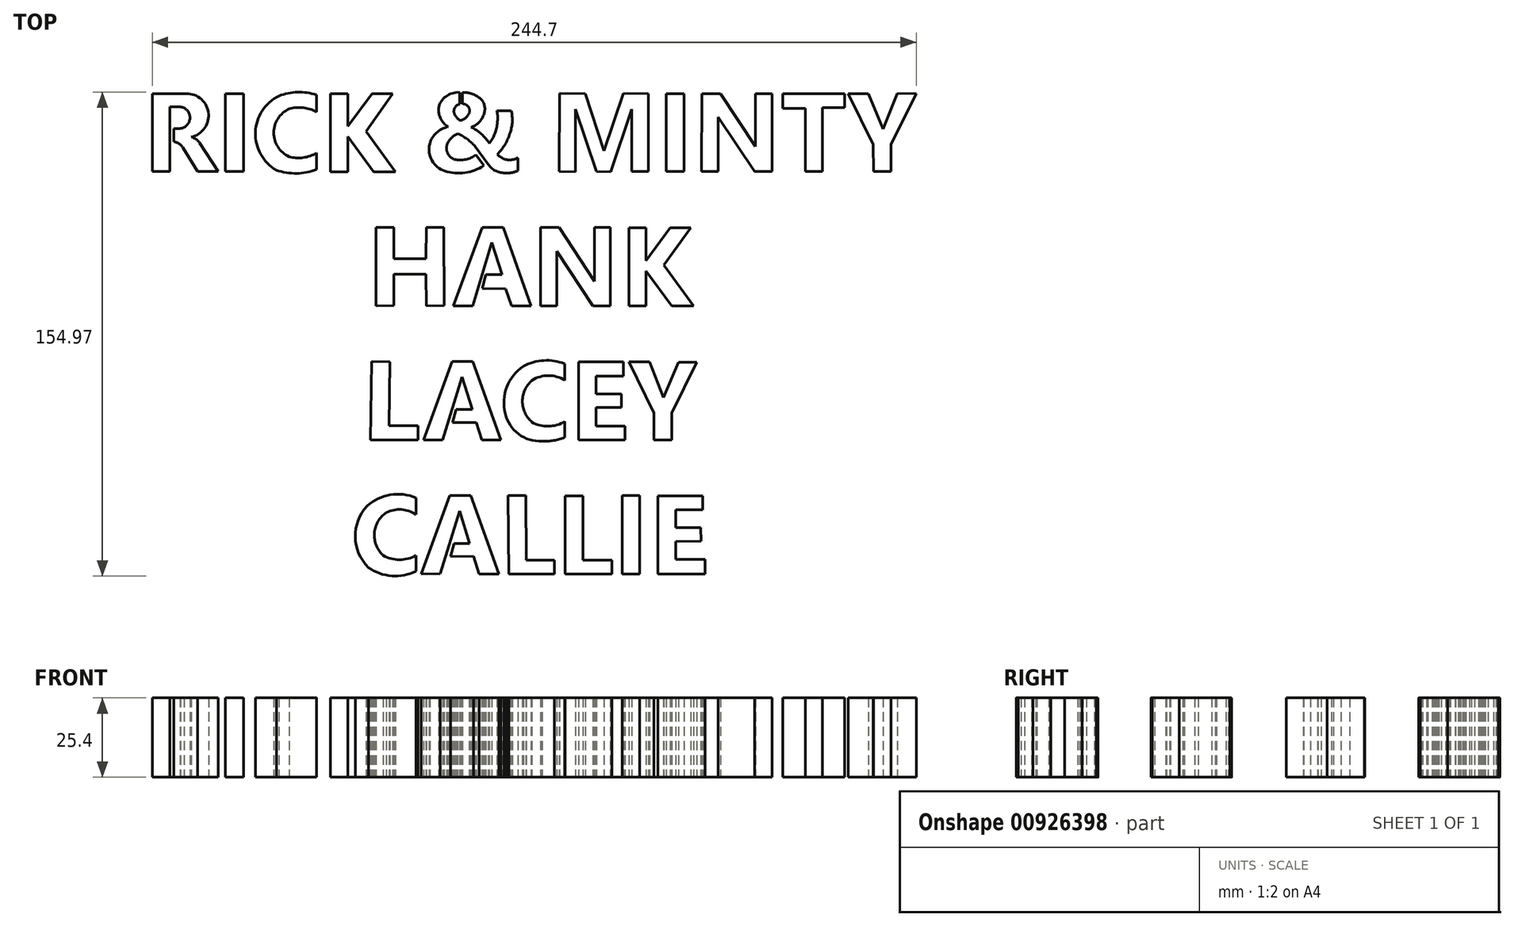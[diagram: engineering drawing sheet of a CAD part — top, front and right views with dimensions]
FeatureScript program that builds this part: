
annotation { "Feature Type Name" : "Feature", "Feature Type Description" : "" }
export const myFeature = defineFeature(function(context is Context, id is Id, definition is map)
    precondition{}
    {
        {
            var Q0;
            Q0=qCreatedBy(makeId("Top.planeOp"),FACE);
            var sketch = newSketch(context, id + "F0", { "sketchPlane" : qUnion([Q0])});
            skLineSegment(sketch, "E0.bottom", {"start": v(49.51, 242.62) * mm, "end": v(55.44, 242.62) * mm});
            skLineSegment(sketch, "E0.top", {"start": v(49.51, 267.6) * mm, "end": v(55.44, 267.6) * mm});
            skLineSegment(sketch, "E0.left", {"start": v(49.51, 242.62) * mm, "end": v(49.51, 267.6) * mm});
            skLineSegment(sketch, "E0.right", {"start": v(55.44, 242.62) * mm, "end": v(55.44, 267.6) * mm});
            skLineSegment(sketch, "E1.bottom", {"start": v(190.8, 242.61) * mm, "end": v(196.47, 242.61) * mm});
            skLineSegment(sketch, "E1.top", {"start": v(190.8, 267.6) * mm, "end": v(196.47, 267.6) * mm});
            skLineSegment(sketch, "E1.left", {"start": v(190.8, 242.61) * mm, "end": v(190.8, 267.6) * mm});
            skLineSegment(sketch, "E1.right", {"start": v(196.47, 242.61) * mm, "end": v(196.47, 267.6) * mm});
            skLineSegment(sketch, "E2.bottom", {"start": v(176.67, 138.96) * mm, "end": v(182.27, 138.96) * mm});
            skLineSegment(sketch, "E2.top", {"start": v(176.67, 113.81) * mm, "end": v(182.27, 113.81) * mm});
            skLineSegment(sketch, "E2.left", {"start": v(176.67, 138.96) * mm, "end": v(176.67, 113.81) * mm});
            skLineSegment(sketch, "E2.right", {"start": v(182.27, 138.96) * mm, "end": v(182.27, 113.81) * mm});
            skLineSegment(sketch, "E3", {"start": v(47.25, 242.62) * mm, "end": v(41.25, 251.83) * mm});
            skLineSegment(sketch, "E4", {"start": v(47.25, 242.62) * mm, "end": v(40.7, 242.62) * mm});
            skLineSegment(sketch, "E5", {"start": v(40.7, 242.62) * mm, "end": v(36, 250.26) * mm});
            skLineSegment(sketch, "E6", {"start": v(33.02, 256.44) * mm, "end": v(33.02, 252.2) * mm});
            skLineSegment(sketch, "E7", {"start": v(31.77, 242.62) * mm, "end": v(31.77, 263.35) * mm});
            skLineSegment(sketch, "E8", {"start": v(31.77, 263.35) * mm, "end": v(35.19, 263.35) * mm});
            skLineSegment(sketch, "E9", {"start": v(33.02, 256.44) * mm, "end": v(35.02, 256.44) * mm});
            skLineSegment(sketch, "E10", {"start": v(31.77, 242.62) * mm, "end": v(26.18, 242.62) * mm});
            skLineSegment(sketch, "E11", {"start": v(26.18, 242.62) * mm, "end": v(26.18, 267.53) * mm});
            skLineSegment(sketch, "E12", {"start": v(26.18, 267.53) * mm, "end": v(36.34, 267.53) * mm});
            skArc(sketch, "E13", {"start": v(35.02, 256.44) * mm, "mid": v(38.21, 259.82) * mm, "end": v(35.19, 263.35) * mm});
            skArc(sketch, "E14", {"start": v(36, 250.26) * mm, "mid": v(34.72, 251.56) * mm, "end": v(33.02, 252.2) * mm});
            skArc(sketch, "E15", {"start": v(41.25, 251.83) * mm, "mid": v(40.1, 253.02) * mm, "end": v(38.58, 253.7) * mm});
            skArc(sketch, "E16", {"start": v(38.58, 253.7) * mm, "mid": v(44.09, 261.7) * mm, "end": v(36.34, 267.53) * mm});
            skArc(sketch, "E17", {"start": v(78.78, 261.7) * mm, "mid": v(74.5, 263.08) * mm, "end": v(70, 262.7) * mm});
            skPoint(sketch, "E17.startSnap0", {"position": v(44.09, 261.7) * mm});
            skArc(sketch, "E18", {"start": v(69.97, 247.4) * mm, "mid": v(74.48, 247.08) * mm, "end": v(78.74, 248.57) * mm});
            skArc(sketch, "E19", {"start": v(70, 262.7) * mm, "mid": v(65.06, 255.06) * mm, "end": v(69.97, 247.4) * mm});
            skArc(sketch, "E20", {"start": v(78.78, 267.16) * mm, "mid": v(72.7, 268.07) * mm, "end": v(66.69, 266.85) * mm});
            skArc(sketch, "E21", {"start": v(65.9, 243.08) * mm, "mid": v(72.34, 242.05) * mm, "end": v(78.74, 243.32) * mm});
            skArc(sketch, "E22", {"start": v(66.69, 266.85) * mm, "mid": v(59.2, 255.2) * mm, "end": v(65.9, 243.08) * mm});
            skLineSegment(sketch, "E23", {"start": v(83.22, 242.5) * mm, "end": v(83.22, 267.52) * mm});
            skLineSegment(sketch, "E24", {"start": v(83.22, 267.52) * mm, "end": v(88.85, 267.52) * mm});
            skLineSegment(sketch, "E25", {"start": v(88.85, 267.52) * mm, "end": v(88.85, 257.13) * mm});
            skLineSegment(sketch, "E26", {"start": v(88.85, 257.13) * mm, "end": v(96.57, 267.52) * mm});
            skLineSegment(sketch, "E27", {"start": v(96.57, 267.52) * mm, "end": v(103.18, 267.52) * mm});
            skLineSegment(sketch, "E28", {"start": v(103.18, 267.52) * mm, "end": v(94.58, 255.52) * mm});
            skLineSegment(sketch, "E29", {"start": v(94.58, 255.52) * mm, "end": v(103.97, 242.54) * mm});
            skLineSegment(sketch, "E30", {"start": v(103.97, 242.54) * mm, "end": v(96.98, 242.54) * mm});
            skLineSegment(sketch, "E31", {"start": v(96.98, 242.54) * mm, "end": v(88.85, 253.87) * mm});
            skLineSegment(sketch, "E32", {"start": v(88.85, 253.87) * mm, "end": v(88.85, 242.54) * mm});
            skLineSegment(sketch, "E33", {"start": v(88.85, 242.54) * mm, "end": v(83.22, 242.5) * mm});
            skLineSegment(sketch, "E34", {"start": v(124.56, 267.99) * mm, "end": v(124.56, 264.22) * mm});
            skLineSegment(sketch, "E35", {"start": v(125.46, 264.31) * mm, "end": v(125.46, 267.97) * mm});
            skArc(sketch, "E36", {"start": v(124.56, 264.22) * mm, "mid": v(123.16, 263.23) * mm, "end": v(122.77, 261.55) * mm});
            skArc(sketch, "E37", {"start": v(122.77, 261.55) * mm, "mid": v(123.56, 260.05) * mm, "end": v(124.9, 259) * mm});
            skArc(sketch, "E38", {"start": v(124.9, 259) * mm, "mid": v(126.57, 259.83) * mm, "end": v(127.66, 261.36) * mm});
            skArc(sketch, "E39", {"start": v(127.66, 261.36) * mm, "mid": v(127.35, 263.42) * mm, "end": v(125.46, 264.31) * mm});
            skArc(sketch, "E40", {"start": v(124.56, 267.99) * mm, "mid": v(120.28, 266.72) * mm, "end": v(117.83, 262.98) * mm});
            skArc(sketch, "E41", {"start": v(117.83, 262.98) * mm, "mid": v(118.54, 259.55) * mm, "end": v(120.89, 256.95) * mm});
            skArc(sketch, "E42", {"start": v(120.89, 256.95) * mm, "mid": v(117.2, 255.07) * mm, "end": v(115.03, 251.53) * mm});
            skArc(sketch, "E43", {"start": v(115.03, 251.53) * mm, "mid": v(115.71, 246.16) * mm, "end": v(119.92, 242.76) * mm});
            skArc(sketch, "E44", {"start": v(119.92, 242.76) * mm, "mid": v(126.33, 242.25) * mm, "end": v(132.34, 244.55) * mm});
            skArc(sketch, "E45", {"start": v(123, 246.5) * mm, "mid": v(126.56, 246.51) * mm, "end": v(129.83, 247.96) * mm});
            skArc(sketch, "E46", {"start": v(120.66, 251.53) * mm, "mid": v(120.74, 248.51) * mm, "end": v(123, 246.5) * mm});
            skArc(sketch, "E47", {"start": v(124.03, 254.74) * mm, "mid": v(122.03, 253.47) * mm, "end": v(120.66, 251.53) * mm});
            skArc(sketch, "E48", {"start": v(129.56, 250.7) * mm, "mid": v(127.01, 253.03) * mm, "end": v(124.03, 254.74) * mm});
            skArc(sketch, "E49", {"start": v(133.72, 244.95) * mm, "mid": v(136.04, 242.9) * mm, "end": v(139.05, 242.2) * mm});
            skArc(sketch, "E50", {"start": v(139.05, 242.2) * mm, "mid": v(141.22, 242.27) * mm, "end": v(143.28, 242.95) * mm});
            skArc(sketch, "E51", {"start": v(139.26, 246.5) * mm, "mid": v(141.33, 246.42) * mm, "end": v(143.3, 247.04) * mm});
            skArc(sketch, "E52", {"start": v(136.65, 248.15) * mm, "mid": v(137.86, 247.18) * mm, "end": v(139.26, 246.5) * mm});
            skArc(sketch, "E53", {"start": v(136.65, 248.15) * mm, "mid": v(139.18, 251.4) * mm, "end": v(140.82, 255.2) * mm});
            skArc(sketch, "E54", {"start": v(140.82, 255.2) * mm, "mid": v(141.46, 258.62) * mm, "end": v(141.14, 262.1) * mm});
            skArc(sketch, "E55", {"start": v(136.65, 258.32) * mm, "mid": v(136.78, 260.23) * mm, "end": v(136.5, 262.12) * mm});
            skArc(sketch, "E56", {"start": v(134.13, 251.69) * mm, "mid": v(135.89, 254.81) * mm, "end": v(136.65, 258.32) * mm});
            skArc(sketch, "E57", {"start": v(134.13, 251.69) * mm, "mid": v(131.57, 254.64) * mm, "end": v(128.31, 256.82) * mm});
            skArc(sketch, "E58", {"start": v(128.31, 256.82) * mm, "mid": v(130.9, 258.48) * mm, "end": v(132.42, 261.17) * mm});
            skArc(sketch, "E59", {"start": v(132.42, 261.17) * mm, "mid": v(132.55, 263.85) * mm, "end": v(131.1, 266.1) * mm});
            skArc(sketch, "E60", {"start": v(131.1, 266.1) * mm, "mid": v(128.45, 267.55) * mm, "end": v(125.46, 267.97) * mm});
            skLineSegment(sketch, "E61", {"start": v(129.83, 247.96) * mm, "end": v(132.34, 244.55) * mm});
            skLineSegment(sketch, "E62", {"start": v(129.56, 250.7) * mm, "end": v(133.72, 244.95) * mm});
            skLineSegment(sketch, "E63", {"start": v(143.28, 242.95) * mm, "end": v(143.3, 247.04) * mm});
            skLineSegment(sketch, "E64", {"start": v(136.5, 262.12) * mm, "end": v(141.14, 262.1) * mm});
            skLineSegment(sketch, "E65", {"start": v(185.07, 242.61) * mm, "end": v(185.07, 267.6) * mm});
            skLineSegment(sketch, "E66", {"start": v(185.07, 267.6) * mm, "end": v(177.1, 267.62) * mm});
            skLineSegment(sketch, "E67", {"start": v(177.1, 267.62) * mm, "end": v(170.85, 249.3) * mm});
            skLineSegment(sketch, "E68", {"start": v(170.85, 249.3) * mm, "end": v(164.84, 267.6) * mm});
            skLineSegment(sketch, "E69", {"start": v(164.84, 267.6) * mm, "end": v(156.64, 267.62) * mm});
            skLineSegment(sketch, "E70", {"start": v(156.64, 267.62) * mm, "end": v(156.54, 242.61) * mm});
            skLineSegment(sketch, "E71", {"start": v(156.54, 242.61) * mm, "end": v(161.72, 242.6) * mm});
            skLineSegment(sketch, "E72", {"start": v(161.72, 242.6) * mm, "end": v(161.72, 262.64) * mm});
            skLineSegment(sketch, "E73", {"start": v(161.72, 262.64) * mm, "end": v(168.36, 242.61) * mm});
            skLineSegment(sketch, "E74", {"start": v(168.36, 242.61) * mm, "end": v(173, 242.6) * mm});
            skLineSegment(sketch, "E75", {"start": v(173, 242.6) * mm, "end": v(179.7, 262.64) * mm});
            skLineSegment(sketch, "E76", {"start": v(179.7, 262.64) * mm, "end": v(179.7, 242.61) * mm});
            skLineSegment(sketch, "E77", {"start": v(179.7, 242.61) * mm, "end": v(185.07, 242.61) * mm});
            skLineSegment(sketch, "E78", {"start": v(202.1, 242.61) * mm, "end": v(202.18, 267.6) * mm});
            skLineSegment(sketch, "E79", {"start": v(202.18, 267.6) * mm, "end": v(208.2, 267.57) * mm});
            skLineSegment(sketch, "E80", {"start": v(208.2, 267.57) * mm, "end": v(219.4, 250.7) * mm});
            skLineSegment(sketch, "E81", {"start": v(219.4, 250.7) * mm, "end": v(219.4, 267.6) * mm});
            skLineSegment(sketch, "E82", {"start": v(219.4, 267.6) * mm, "end": v(224.69, 267.57) * mm});
            skLineSegment(sketch, "E83", {"start": v(224.69, 267.57) * mm, "end": v(224.69, 242.61) * mm});
            skLineSegment(sketch, "E84", {"start": v(224.69, 242.61) * mm, "end": v(219.05, 242.63) * mm});
            skLineSegment(sketch, "E85", {"start": v(219.05, 242.63) * mm, "end": v(207.44, 260.02) * mm});
            skLineSegment(sketch, "E86", {"start": v(207.44, 260.02) * mm, "end": v(207.44, 242.61) * mm});
            skLineSegment(sketch, "E87", {"start": v(207.44, 242.61) * mm, "end": v(202.1, 242.61) * mm});
            skLineSegment(sketch, "E88", {"start": v(228.12, 267.6) * mm, "end": v(247.98, 267.52) * mm});
            skLineSegment(sketch, "E89", {"start": v(247.98, 267.52) * mm, "end": v(247.98, 263.1) * mm});
            skLineSegment(sketch, "E90", {"start": v(247.98, 263.1) * mm, "end": v(240.84, 263.12) * mm});
            skLineSegment(sketch, "E91", {"start": v(240.84, 263.12) * mm, "end": v(240.84, 242.61) * mm});
            skLineSegment(sketch, "E92", {"start": v(240.84, 242.61) * mm, "end": v(235.32, 242.63) * mm});
            skLineSegment(sketch, "E93", {"start": v(235.32, 242.63) * mm, "end": v(235.32, 262.86) * mm});
            skLineSegment(sketch, "E94", {"start": v(235.32, 262.86) * mm, "end": v(228.12, 262.9) * mm});
            skLineSegment(sketch, "E95", {"start": v(228.12, 262.9) * mm, "end": v(228.12, 267.6) * mm});
            skLineSegment(sketch, "E96", {"start": v(249.05, 267.57) * mm, "end": v(255.54, 267.55) * mm});
            skLineSegment(sketch, "E97", {"start": v(255.54, 267.55) * mm, "end": v(260.2, 256.2) * mm});
            skLineSegment(sketch, "E98", {"start": v(260.2, 256.2) * mm, "end": v(264.87, 267.64) * mm});
            skLineSegment(sketch, "E99", {"start": v(264.87, 267.64) * mm, "end": v(270.88, 267.57) * mm});
            skLineSegment(sketch, "E100", {"start": v(270.88, 267.57) * mm, "end": v(262.76, 251.37) * mm});
            skLineSegment(sketch, "E101", {"start": v(262.76, 251.37) * mm, "end": v(262.72, 242.6) * mm});
            skLineSegment(sketch, "E102", {"start": v(262.72, 242.6) * mm, "end": v(257.18, 242.63) * mm});
            skLineSegment(sketch, "E103", {"start": v(257.18, 242.63) * mm, "end": v(257.1, 251.32) * mm});
            skLineSegment(sketch, "E104", {"start": v(257.1, 251.32) * mm, "end": v(249.05, 267.57) * mm});
            skLineSegment(sketch, "E105", {"start": v(97.85, 199.62) * mm, "end": v(97.85, 224.72) * mm});
            skLineSegment(sketch, "E106", {"start": v(97.85, 224.72) * mm, "end": v(103.54, 224.72) * mm});
            skLineSegment(sketch, "E107", {"start": v(103.54, 224.72) * mm, "end": v(103.54, 214.72) * mm});
            skLineSegment(sketch, "E108", {"start": v(103.54, 214.72) * mm, "end": v(113.87, 214.72) * mm});
            skLineSegment(sketch, "E109", {"start": v(113.87, 214.72) * mm, "end": v(113.99, 224.72) * mm});
            skLineSegment(sketch, "E110", {"start": v(113.99, 224.72) * mm, "end": v(119.56, 224.72) * mm});
            skLineSegment(sketch, "E111", {"start": v(119.56, 224.72) * mm, "end": v(119.62, 199.68) * mm});
            skLineSegment(sketch, "E112", {"start": v(119.62, 199.68) * mm, "end": v(113.93, 199.66) * mm});
            skLineSegment(sketch, "E113", {"start": v(113.93, 199.66) * mm, "end": v(113.82, 209.73) * mm});
            skLineSegment(sketch, "E114", {"start": v(113.82, 209.73) * mm, "end": v(103.54, 209.78) * mm});
            skLineSegment(sketch, "E115", {"start": v(103.54, 209.78) * mm, "end": v(103.48, 199.68) * mm});
            skLineSegment(sketch, "E116", {"start": v(103.48, 199.68) * mm, "end": v(97.85, 199.62) * mm});
            skLineSegment(sketch, "E117", {"start": v(122.6, 199.62) * mm, "end": v(131.8, 224.72) * mm});
            skLineSegment(sketch, "E118", {"start": v(131.8, 224.72) * mm, "end": v(138.51, 224.72) * mm});
            skLineSegment(sketch, "E119", {"start": v(138.51, 224.72) * mm, "end": v(147.41, 199.62) * mm});
            skLineSegment(sketch, "E120", {"start": v(147.41, 199.62) * mm, "end": v(141.21, 199.62) * mm});
            skLineSegment(sketch, "E121", {"start": v(141.21, 199.62) * mm, "end": v(139.37, 205.13) * mm});
            skLineSegment(sketch, "E122", {"start": v(139.37, 205.13) * mm, "end": v(131.9, 205.25) * mm});
            skLineSegment(sketch, "E123", {"start": v(131.9, 205.25) * mm, "end": v(133, 209.61) * mm});
            skLineSegment(sketch, "E124", {"start": v(133, 209.61) * mm, "end": v(138.17, 209.61) * mm});
            skLineSegment(sketch, "E125", {"start": v(138.17, 209.61) * mm, "end": v(134.84, 219.95) * mm});
            skLineSegment(sketch, "E126", {"start": v(134.84, 219.95) * mm, "end": v(128.75, 199.62) * mm});
            skLineSegment(sketch, "E127", {"start": v(128.75, 199.62) * mm, "end": v(122.6, 199.62) * mm});
            skLineSegment(sketch, "E128", {"start": v(150.46, 199.62) * mm, "end": v(150.46, 224.72) * mm});
            skLineSegment(sketch, "E129", {"start": v(150.46, 224.72) * mm, "end": v(156.49, 224.72) * mm});
            skLineSegment(sketch, "E130", {"start": v(156.49, 224.72) * mm, "end": v(167.74, 207.43) * mm});
            skLineSegment(sketch, "E131", {"start": v(167.74, 207.43) * mm, "end": v(167.74, 224.72) * mm});
            skLineSegment(sketch, "E132", {"start": v(167.74, 224.72) * mm, "end": v(172.86, 224.72) * mm});
            skLineSegment(sketch, "E133", {"start": v(172.86, 224.72) * mm, "end": v(172.86, 199.62) * mm});
            skLineSegment(sketch, "E134", {"start": v(172.86, 199.62) * mm, "end": v(167.28, 199.62) * mm});
            skLineSegment(sketch, "E135", {"start": v(167.28, 199.62) * mm, "end": v(155.68, 217.2) * mm});
            skLineSegment(sketch, "E136", {"start": v(155.68, 217.2) * mm, "end": v(155.68, 199.62) * mm});
            skLineSegment(sketch, "E137", {"start": v(155.68, 199.62) * mm, "end": v(150.46, 199.62) * mm});
            skLineSegment(sketch, "E138", {"start": v(178.77, 199.62) * mm, "end": v(178.77, 224.66) * mm});
            skLineSegment(sketch, "E139", {"start": v(178.77, 224.66) * mm, "end": v(184.34, 224.66) * mm});
            skLineSegment(sketch, "E140", {"start": v(184.34, 224.66) * mm, "end": v(184.34, 214.15) * mm});
            skLineSegment(sketch, "E141", {"start": v(184.34, 214.15) * mm, "end": v(191.98, 224.6) * mm});
            skLineSegment(sketch, "E142", {"start": v(191.98, 224.6) * mm, "end": v(198.7, 224.6) * mm});
            skLineSegment(sketch, "E143", {"start": v(198.7, 224.6) * mm, "end": v(189.97, 212.71) * mm});
            skLineSegment(sketch, "E144", {"start": v(189.97, 212.71) * mm, "end": v(199.56, 199.62) * mm});
            skLineSegment(sketch, "E145", {"start": v(199.56, 199.62) * mm, "end": v(192.55, 199.62) * mm});
            skLineSegment(sketch, "E146", {"start": v(192.55, 199.62) * mm, "end": v(184.34, 210.82) * mm});
            skLineSegment(sketch, "E147", {"start": v(184.34, 210.82) * mm, "end": v(184.34, 199.62) * mm});
            skLineSegment(sketch, "E148", {"start": v(184.34, 199.62) * mm, "end": v(178.77, 199.62) * mm});
            skLineSegment(sketch, "E149", {"start": v(78.74, 243.32) * mm, "end": v(78.74, 248.57) * mm});
            skLineSegment(sketch, "E150", {"start": v(78.78, 267.16) * mm, "end": v(78.78, 261.7) * mm});
            skLineSegment(sketch, "E151", {"start": v(96.37, 181.8) * mm, "end": v(96.08, 156.74) * mm});
            skLineSegment(sketch, "E152", {"start": v(96.08, 156.74) * mm, "end": v(111.33, 156.74) * mm});
            skLineSegment(sketch, "E153", {"start": v(111.33, 156.74) * mm, "end": v(111.28, 161.25) * mm});
            skLineSegment(sketch, "E154", {"start": v(111.28, 161.25) * mm, "end": v(101.97, 161.25) * mm});
            skLineSegment(sketch, "E155", {"start": v(101.97, 161.25) * mm, "end": v(102.2, 181.67) * mm});
            skLineSegment(sketch, "E156", {"start": v(102.2, 181.67) * mm, "end": v(96.37, 181.8) * mm});
            skLineSegment(sketch, "E157", {"start": v(113.07, 156.74) * mm, "end": v(122.25, 181.8) * mm});
            skLineSegment(sketch, "E158", {"start": v(122.25, 181.8) * mm, "end": v(128.83, 181.8) * mm});
            skLineSegment(sketch, "E159", {"start": v(128.83, 181.8) * mm, "end": v(137.8, 156.74) * mm});
            skLineSegment(sketch, "E160", {"start": v(137.8, 156.74) * mm, "end": v(131.71, 156.74) * mm});
            skLineSegment(sketch, "E161", {"start": v(131.71, 156.74) * mm, "end": v(129.92, 162.26) * mm});
            skLineSegment(sketch, "E162", {"start": v(129.92, 162.26) * mm, "end": v(122.35, 162.26) * mm});
            skLineSegment(sketch, "E163", {"start": v(122.35, 162.26) * mm, "end": v(123.4, 166.47) * mm});
            skLineSegment(sketch, "E164", {"start": v(123.4, 166.47) * mm, "end": v(128.62, 166.47) * mm});
            skLineSegment(sketch, "E165", {"start": v(128.62, 166.47) * mm, "end": v(125.32, 176.89) * mm});
            skLineSegment(sketch, "E166", {"start": v(125.32, 176.89) * mm, "end": v(119.15, 156.74) * mm});
            skLineSegment(sketch, "E167", {"start": v(119.15, 156.74) * mm, "end": v(113.07, 156.74) * mm});
            skLineSegment(sketch, "E168", {"start": v(158.3, 175.78) * mm, "end": v(158.24, 181.1) * mm});
            skLineSegment(sketch, "E169", {"start": v(158.3, 162.6) * mm, "end": v(158.3, 157.51) * mm});
            skArc(sketch, "E170", {"start": v(158.3, 175.78) * mm, "mid": v(153.05, 177.3) * mm, "end": v(147.79, 175.78) * mm});
            skArc(sketch, "E171", {"start": v(147.79, 175.78) * mm, "mid": v(144.7, 169.09) * mm, "end": v(147.79, 162.4) * mm});
            skArc(sketch, "E172", {"start": v(147.79, 162.4) * mm, "mid": v(153.07, 161.07) * mm, "end": v(158.3, 162.6) * mm});
            skArc(sketch, "E173", {"start": v(158.24, 181.1) * mm, "mid": v(151.57, 182.13) * mm, "end": v(145.06, 180.32) * mm});
            skArc(sketch, "E174", {"start": v(145.06, 180.32) * mm, "mid": v(139.73, 173.67) * mm, "end": v(139.25, 165.16) * mm});
            skArc(sketch, "E175", {"start": v(139.25, 165.16) * mm, "mid": v(143.48, 158.56) * mm, "end": v(151, 156.32) * mm});
            skArc(sketch, "E176", {"start": v(151, 156.32) * mm, "mid": v(154.71, 156.53) * mm, "end": v(158.3, 157.51) * mm});
            skLineSegment(sketch, "E177", {"start": v(162.68, 156.66) * mm, "end": v(162.68, 181.69) * mm});
            skLineSegment(sketch, "E178", {"start": v(162.68, 181.69) * mm, "end": v(177.09, 181.69) * mm});
            skLineSegment(sketch, "E179", {"start": v(177.09, 181.69) * mm, "end": v(177.09, 177.11) * mm});
            skLineSegment(sketch, "E180", {"start": v(177.09, 177.11) * mm, "end": v(168.31, 177.11) * mm});
            skLineSegment(sketch, "E181", {"start": v(168.31, 177.11) * mm, "end": v(168.31, 171.38) * mm});
            skLineSegment(sketch, "E182", {"start": v(168.31, 171.38) * mm, "end": v(176.44, 171.38) * mm});
            skLineSegment(sketch, "E183", {"start": v(176.44, 171.38) * mm, "end": v(176.44, 167.04) * mm});
            skLineSegment(sketch, "E184", {"start": v(176.44, 167.04) * mm, "end": v(168.31, 167.04) * mm});
            skLineSegment(sketch, "E185", {"start": v(168.31, 167.04) * mm, "end": v(168.31, 161.17) * mm});
            skLineSegment(sketch, "E186", {"start": v(168.31, 161.17) * mm, "end": v(177.57, 161.17) * mm});
            skLineSegment(sketch, "E187", {"start": v(177.57, 161.17) * mm, "end": v(177.57, 156.7) * mm});
            skLineSegment(sketch, "E188", {"start": v(177.57, 156.7) * mm, "end": v(162.68, 156.66) * mm});
            skLineSegment(sketch, "E189", {"start": v(186.85, 156.66) * mm, "end": v(186.85, 165.33) * mm});
            skLineSegment(sketch, "E190", {"start": v(186.85, 165.33) * mm, "end": v(178.86, 181.66) * mm});
            skLineSegment(sketch, "E191", {"start": v(178.86, 181.66) * mm, "end": v(185.39, 181.66) * mm});
            skLineSegment(sketch, "E192", {"start": v(185.39, 181.66) * mm, "end": v(189.93, 170.28) * mm});
            skLineSegment(sketch, "E193", {"start": v(189.93, 170.28) * mm, "end": v(194.67, 181.62) * mm});
            skLineSegment(sketch, "E194", {"start": v(194.67, 181.62) * mm, "end": v(200.58, 181.62) * mm});
            skLineSegment(sketch, "E195", {"start": v(200.58, 181.62) * mm, "end": v(192.49, 165.37) * mm});
            skLineSegment(sketch, "E196", {"start": v(192.49, 165.37) * mm, "end": v(192.49, 156.66) * mm});
            skLineSegment(sketch, "E197", {"start": v(192.49, 156.66) * mm, "end": v(186.85, 156.66) * mm});
            skLineSegment(sketch, "E198", {"start": v(188.15, 113.81) * mm, "end": v(188.1, 138.73) * mm});
            skLineSegment(sketch, "E199", {"start": v(188.1, 138.73) * mm, "end": v(202.5, 138.76) * mm});
            skLineSegment(sketch, "E200", {"start": v(202.5, 138.76) * mm, "end": v(202.5, 134.29) * mm});
            skLineSegment(sketch, "E201", {"start": v(202.5, 134.29) * mm, "end": v(193.82, 134.27) * mm});
            skLineSegment(sketch, "E202", {"start": v(193.82, 134.27) * mm, "end": v(193.83, 128.62) * mm});
            skLineSegment(sketch, "E203", {"start": v(193.83, 128.62) * mm, "end": v(201.88, 128.64) * mm});
            skLineSegment(sketch, "E204", {"start": v(201.88, 128.64) * mm, "end": v(201.89, 124.25) * mm});
            skLineSegment(sketch, "E205", {"start": v(201.89, 124.25) * mm, "end": v(193.83, 124.23) * mm});
            skLineSegment(sketch, "E206", {"start": v(193.83, 124.23) * mm, "end": v(193.84, 118.44) * mm});
            skLineSegment(sketch, "E207", {"start": v(193.84, 118.44) * mm, "end": v(203.18, 118.47) * mm});
            skLineSegment(sketch, "E208", {"start": v(203.18, 118.47) * mm, "end": v(203.19, 113.81) * mm});
            skLineSegment(sketch, "E209", {"start": v(203.19, 113.81) * mm, "end": v(188.15, 113.81) * mm});
            skLineSegment(sketch, "E210", {"start": v(173.4, 113.81) * mm, "end": v(173.39, 118.17) * mm});
            skLineSegment(sketch, "E211", {"start": v(173.39, 118.17) * mm, "end": v(164.1, 118.15) * mm});
            skLineSegment(sketch, "E212", {"start": v(164.1, 118.15) * mm, "end": v(164.06, 138.73) * mm});
            skLineSegment(sketch, "E213", {"start": v(164.06, 138.73) * mm, "end": v(158.37, 138.71) * mm});
            skLineSegment(sketch, "E214", {"start": v(158.37, 138.71) * mm, "end": v(158.43, 113.81) * mm});
            skLineSegment(sketch, "E215", {"start": v(158.43, 113.81) * mm, "end": v(173.4, 113.81) * mm});
            skLineSegment(sketch, "E216", {"start": v(140.14, 138.93) * mm, "end": v(145.87, 138.95) * mm});
            skLineSegment(sketch, "E217", {"start": v(145.87, 138.95) * mm, "end": v(145.92, 118.24) * mm});
            skLineSegment(sketch, "E218", {"start": v(145.92, 118.24) * mm, "end": v(154.96, 118.26) * mm});
            skLineSegment(sketch, "E219", {"start": v(154.96, 118.26) * mm, "end": v(154.97, 113.81) * mm});
            skLineSegment(sketch, "E220", {"start": v(154.97, 113.81) * mm, "end": v(140.34, 113.78) * mm});
            skLineSegment(sketch, "E221", {"start": v(140.34, 113.78) * mm, "end": v(140.14, 138.93) * mm});
            skLineSegment(sketch, "E222", {"start": v(137.13, 113.81) * mm, "end": v(128.14, 138.93) * mm});
            skLineSegment(sketch, "E223", {"start": v(128.14, 138.93) * mm, "end": v(121.42, 138.92) * mm});
            skLineSegment(sketch, "E224", {"start": v(121.42, 138.92) * mm, "end": v(112.27, 113.81) * mm});
            skLineSegment(sketch, "E225", {"start": v(112.27, 113.81) * mm, "end": v(118.42, 113.83) * mm});
            skLineSegment(sketch, "E226", {"start": v(118.42, 113.83) * mm, "end": v(124.63, 133.95) * mm});
            skLineSegment(sketch, "E227", {"start": v(124.63, 133.95) * mm, "end": v(127.8, 123.53) * mm});
            skLineSegment(sketch, "E228", {"start": v(127.8, 123.53) * mm, "end": v(122.86, 123.52) * mm});
            skLineSegment(sketch, "E229", {"start": v(122.86, 123.52) * mm, "end": v(121.66, 119.4) * mm});
            skLineSegment(sketch, "E230", {"start": v(121.66, 119.4) * mm, "end": v(129.1, 119.42) * mm});
            skLineSegment(sketch, "E231", {"start": v(129.1, 119.42) * mm, "end": v(130.81, 113.81) * mm});
            skLineSegment(sketch, "E232", {"start": v(130.81, 113.81) * mm, "end": v(137.13, 113.81) * mm});
            skLineSegment(sketch, "E233", {"start": v(110.64, 114.62) * mm, "end": v(110.63, 119.7) * mm});
            skLineSegment(sketch, "E234", {"start": v(110.6, 132.86) * mm, "end": v(110.6, 138.15) * mm});
            skArc(sketch, "E235", {"start": v(100.09, 119.7) * mm, "mid": v(105.36, 118.32) * mm, "end": v(110.63, 119.7) * mm});
            skArc(sketch, "E236", {"start": v(110.6, 132.86) * mm, "mid": v(105.95, 134.4) * mm, "end": v(101.14, 133.47) * mm});
            skArc(sketch, "E237", {"start": v(101.14, 133.47) * mm, "mid": v(97.3, 126.84) * mm, "end": v(100.09, 119.7) * mm});
            skArc(sketch, "E238", {"start": v(110.6, 138.15) * mm, "mid": v(102.41, 139.14) * mm, "end": v(94.96, 135.59) * mm});
            skArc(sketch, "E239", {"start": v(95.37, 115.85) * mm, "mid": v(102.84, 113.16) * mm, "end": v(110.64, 114.62) * mm});
            skArc(sketch, "E240", {"start": v(94.96, 135.59) * mm, "mid": v(91.17, 125.64) * mm, "end": v(95.37, 115.85) * mm});
            skSolve(sketch);
        }
        {
            var Q0;
            Q0=makeQuery(id+"F0.imprint","IMPRINT",FACE,{"disambiguationData":[TD([[makeQuery(id+"F0.imprint","IMPRINT",EDGE,{"derivedFrom":sQuery(id+"F0.wireOp",EDGE,"E3")}),1.0]])]});
            var Q1;
            Q1=makeQuery(id+"F0.imprint","IMPRINT",FACE,{"disambiguationData":[TD([[makeQuery(id+"F0.imprint","IMPRINT",EDGE,{"derivedFrom":sQuery(id+"F0.wireOp",EDGE,"E0.bottom")}),1.0]])]});
            var Q2;
            Q2=makeQuery(id+"F0.imprint","IMPRINT",FACE,{"disambiguationData":[TD([[makeQuery(id+"F0.imprint","IMPRINT",EDGE,{"derivedFrom":sQuery(id+"F0.wireOp",EDGE,"E17")}),-1.0]])]});
            var Q3;
            Q3=makeQuery(id+"F0.imprint","IMPRINT",FACE,{"disambiguationData":[TD([[makeQuery(id+"F0.imprint","IMPRINT",EDGE,{"derivedFrom":sQuery(id+"F0.wireOp",EDGE,"E23")}),-1.0]])]});
            var Q4;
            Q4=makeQuery(id+"F0.imprint","IMPRINT",FACE,{"disambiguationData":[TD([[makeQuery(id+"F0.imprint","IMPRINT",EDGE,{"derivedFrom":sQuery(id+"F0.wireOp",EDGE,"E34")}),-1.0]])]});
            var Q5;
            Q5=makeQuery(id+"F0.imprint","IMPRINT",FACE,{"disambiguationData":[TD([[makeQuery(id+"F0.imprint","IMPRINT",EDGE,{"derivedFrom":sQuery(id+"F0.wireOp",EDGE,"E65")}),1.0]])]});
            var Q6;
            Q6=makeQuery(id+"F0.imprint","IMPRINT",FACE,{"disambiguationData":[TD([[makeQuery(id+"F0.imprint","IMPRINT",EDGE,{"derivedFrom":sQuery(id+"F0.wireOp",EDGE,"E1.bottom")}),1.0]])]});
            var Q7;
            Q7=makeQuery(id+"F0.imprint","IMPRINT",FACE,{"disambiguationData":[TD([[makeQuery(id+"F0.imprint","IMPRINT",EDGE,{"derivedFrom":sQuery(id+"F0.wireOp",EDGE,"E78")}),-1.0]])]});
            var Q8;
            Q8=makeQuery(id+"F0.imprint","IMPRINT",FACE,{"disambiguationData":[TD([[makeQuery(id+"F0.imprint","IMPRINT",EDGE,{"derivedFrom":sQuery(id+"F0.wireOp",EDGE,"E88")}),-1.0]])]});
            var Q9;
            Q9=makeQuery(id+"F0.imprint","IMPRINT",FACE,{"disambiguationData":[TD([[makeQuery(id+"F0.imprint","IMPRINT",EDGE,{"derivedFrom":sQuery(id+"F0.wireOp",EDGE,"E96")}),-1.0]])]});
            var Q10;
            Q10=makeQuery(id+"F0.imprint","IMPRINT",FACE,{"disambiguationData":[TD([[makeQuery(id+"F0.imprint","IMPRINT",EDGE,{"derivedFrom":sQuery(id+"F0.wireOp",EDGE,"E105")}),-1.0]])]});
            var Q11;
            Q11=makeQuery(id+"F0.imprint","IMPRINT",FACE,{"disambiguationData":[TD([[makeQuery(id+"F0.imprint","IMPRINT",EDGE,{"derivedFrom":sQuery(id+"F0.wireOp",EDGE,"E117")}),-1.0]])]});
            var Q12;
            Q12=makeQuery(id+"F0.imprint","IMPRINT",FACE,{"disambiguationData":[TD([[makeQuery(id+"F0.imprint","IMPRINT",EDGE,{"derivedFrom":sQuery(id+"F0.wireOp",EDGE,"E128")}),-1.0]])]});
            var Q13;
            Q13=makeQuery(id+"F0.imprint","IMPRINT",FACE,{"disambiguationData":[TD([[makeQuery(id+"F0.imprint","IMPRINT",EDGE,{"derivedFrom":sQuery(id+"F0.wireOp",EDGE,"E138")}),-1.0]])]});
            var Q14;
            Q14=makeQuery(id+"F0.imprint","IMPRINT",FACE,{"disambiguationData":[TD([[makeQuery(id+"F0.imprint","IMPRINT",EDGE,{"derivedFrom":sQuery(id+"F0.wireOp",EDGE,"E151")}),1.0]])]});
            var Q15;
            Q15=makeQuery(id+"F0.imprint","IMPRINT",FACE,{"disambiguationData":[TD([[makeQuery(id+"F0.imprint","IMPRINT",EDGE,{"derivedFrom":sQuery(id+"F0.wireOp",EDGE,"E157")}),-1.0]])]});
            var Q16;
            Q16=makeQuery(id+"F0.imprint","IMPRINT",FACE,{"disambiguationData":[TD([[makeQuery(id+"F0.imprint","IMPRINT",EDGE,{"derivedFrom":sQuery(id+"F0.wireOp",EDGE,"E168")}),1.0]])]});
            var Q17;
            Q17=makeQuery(id+"F0.imprint","IMPRINT",FACE,{"disambiguationData":[TD([[makeQuery(id+"F0.imprint","IMPRINT",EDGE,{"derivedFrom":sQuery(id+"F0.wireOp",EDGE,"E177")}),-1.0]])]});
            var Q18;
            Q18=makeQuery(id+"F0.imprint","IMPRINT",FACE,{"disambiguationData":[TD([[makeQuery(id+"F0.imprint","IMPRINT",EDGE,{"derivedFrom":sQuery(id+"F0.wireOp",EDGE,"E189")}),-1.0]])]});
            var Q19;
            Q19=makeQuery(id+"F0.imprint","IMPRINT",FACE,{"disambiguationData":[TD([[makeQuery(id+"F0.imprint","IMPRINT",EDGE,{"derivedFrom":sQuery(id+"F0.wireOp",EDGE,"E233")}),1.0]])]});
            var Q20;
            Q20=makeQuery(id+"F0.imprint","IMPRINT",FACE,{"disambiguationData":[TD([[makeQuery(id+"F0.imprint","IMPRINT",EDGE,{"derivedFrom":sQuery(id+"F0.wireOp",EDGE,"E222")}),1.0]])]});
            var Q21;
            Q21=makeQuery(id+"F0.imprint","IMPRINT",FACE,{"disambiguationData":[TD([[makeQuery(id+"F0.imprint","IMPRINT",EDGE,{"derivedFrom":sQuery(id+"F0.wireOp",EDGE,"E216")}),-1.0]])]});
            var Q22;
            Q22=makeQuery(id+"F0.imprint","IMPRINT",FACE,{"disambiguationData":[TD([[makeQuery(id+"F0.imprint","IMPRINT",EDGE,{"derivedFrom":sQuery(id+"F0.wireOp",EDGE,"E210")}),1.0]])]});
            var Q23;
            Q23=makeQuery(id+"F0.imprint","IMPRINT",FACE,{"disambiguationData":[TD([[makeQuery(id+"F0.imprint","IMPRINT",EDGE,{"derivedFrom":sQuery(id+"F0.wireOp",EDGE,"E2.bottom")}),-1.0]])]});
            var Q24;
            Q24=makeQuery(id+"F0.imprint","IMPRINT",FACE,{"disambiguationData":[TD([[makeQuery(id+"F0.imprint","IMPRINT",EDGE,{"derivedFrom":sQuery(id+"F0.wireOp",EDGE,"E198")}),-1.0]])]});
            extrude(context, id + "F1", {"entities" : qUnion([Q0, Q1, Q2, Q3, Q4, Q5, Q6, Q7, Q8, Q9, Q10, Q11, Q12, Q13, Q14, Q15, Q16, Q17, Q18, Q19, Q20, Q21, Q22, Q23, Q24]), "depth" : 25.4 * mm, "offsetDistance" : 25.4 * mm});
        }
    });
